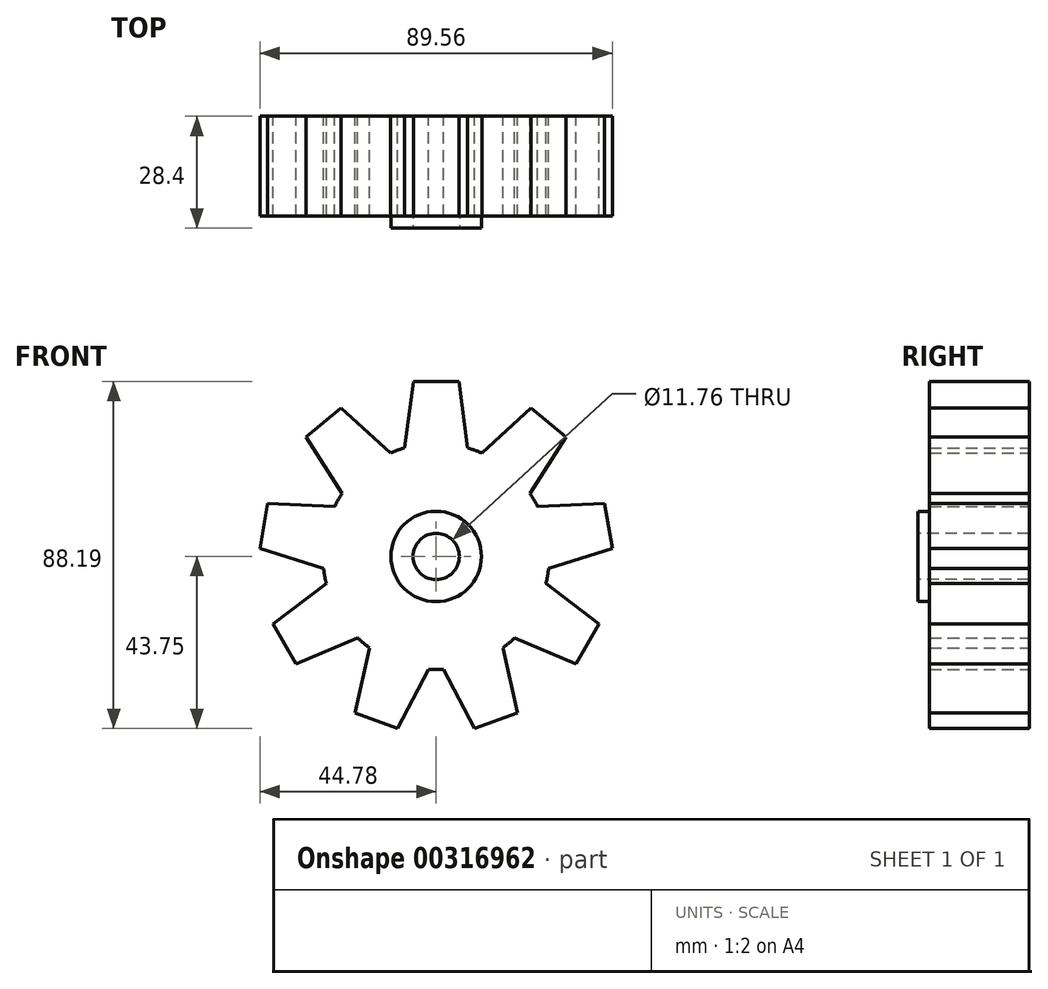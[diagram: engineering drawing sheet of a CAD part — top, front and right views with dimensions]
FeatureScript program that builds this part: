
annotation { "Feature Type Name" : "Feature", "Feature Type Description" : "" }
export const myFeature = defineFeature(function(context is Context, id is Id, definition is map)
    precondition{}
    {
        {
            var Q0;
            Q0=qCreatedBy(makeId("Front.planeOp"),FACE);
            var sketch = newSketch(context, id + "F0", { "sketchPlane" : qUnion([Q0])});
            skCircle(sketch, "E0", {"center": v(0, 0) * mm, "radius": 28.73 * mm});
            skLineSegment(sketch, "E1", {"start": v(0, 44.44) * mm, "end": v(0, 44.44) * mm});
            skLineSegment(sketch, "E2", {"start": v(0, 44.44) * mm, "end": v(5.8, 44.44) * mm});
            skLineSegment(sketch, "E3", {"start": v(5.8, 44.44) * mm, "end": v(8, 27.6) * mm});
            skLineSegment(sketch, "E4.MirrorCS", {"start": v(-5.8, 44.44) * mm, "end": v(-8, 27.6) * mm});
            skLineSegment(sketch, "E5.MirrorCS", {"start": v(0, 44.44) * mm, "end": v(-5.8, 44.44) * mm});
            skPoint(sketch, "E6.start.orphan", {"position": v(11.59, 0) * mm});
            skPoint(sketch, "E7.MirrorCS.start.orphan", {"position": v(-11.59, 0) * mm});
            skPoint(sketch, "E8.MirrorCS.start.orphan", {"position": v(0, 44.44) * mm});
            skLineSegment(sketch, "E9.1.0", {"start": v(28.57, 34.05) * mm, "end": v(33, 30.32) * mm});
            skLineSegment(sketch, "E9.1.1", {"start": v(33, 30.32) * mm, "end": v(23.86, 16) * mm});
            skLineSegment(sketch, "E9.1.2", {"start": v(24.13, 37.77) * mm, "end": v(11.62, 26.28) * mm});
            skLineSegment(sketch, "E9.1.3", {"start": v(28.57, 34.05) * mm, "end": v(24.13, 37.77) * mm});
            skLineSegment(sketch, "E9.2.0", {"start": v(43.77, 7.72) * mm, "end": v(44.78, 2) * mm});
            skLineSegment(sketch, "E9.2.1", {"start": v(44.78, 2) * mm, "end": v(28.57, -3.08) * mm});
            skLineSegment(sketch, "E9.2.2", {"start": v(42.76, 13.43) * mm, "end": v(25.8, 12.66) * mm});
            skLineSegment(sketch, "E9.2.3", {"start": v(43.77, 7.72) * mm, "end": v(42.76, 13.43) * mm});
            skLineSegment(sketch, "E9.3.0", {"start": v(38.5, -22.22) * mm, "end": v(35.6, -27.24) * mm});
            skLineSegment(sketch, "E9.3.1", {"start": v(35.6, -27.24) * mm, "end": v(19.9, -20.72) * mm});
            skLineSegment(sketch, "E9.3.2", {"start": v(41.39, -17.2) * mm, "end": v(27.9, -6.88) * mm});
            skLineSegment(sketch, "E9.3.3", {"start": v(38.5, -22.22) * mm, "end": v(41.39, -17.2) * mm});
            skLineSegment(sketch, "E9.4.0", {"start": v(15.2, -41.76) * mm, "end": v(9.75, -43.75) * mm});
            skLineSegment(sketch, "E9.4.1", {"start": v(9.75, -43.75) * mm, "end": v(1.93, -28.67) * mm});
            skLineSegment(sketch, "E9.4.2", {"start": v(20.65, -39.78) * mm, "end": v(16.95, -23.2) * mm});
            skLineSegment(sketch, "E9.4.3", {"start": v(15.2, -41.76) * mm, "end": v(20.65, -39.78) * mm});
            skLineSegment(sketch, "E9.5.0", {"start": v(-15.2, -41.76) * mm, "end": v(-20.65, -39.78) * mm});
            skLineSegment(sketch, "E9.5.1", {"start": v(-20.65, -39.78) * mm, "end": v(-16.95, -23.2) * mm});
            skLineSegment(sketch, "E9.5.2", {"start": v(-9.75, -43.75) * mm, "end": v(-1.93, -28.67) * mm});
            skLineSegment(sketch, "E9.5.3", {"start": v(-15.2, -41.76) * mm, "end": v(-9.75, -43.75) * mm});
            skLineSegment(sketch, "E9.6.0", {"start": v(-38.5, -22.22) * mm, "end": v(-41.39, -17.2) * mm});
            skLineSegment(sketch, "E9.6.1", {"start": v(-41.39, -17.2) * mm, "end": v(-27.9, -6.88) * mm});
            skLineSegment(sketch, "E9.6.2", {"start": v(-35.6, -27.24) * mm, "end": v(-19.9, -20.72) * mm});
            skLineSegment(sketch, "E9.6.3", {"start": v(-38.5, -22.22) * mm, "end": v(-35.6, -27.24) * mm});
            skLineSegment(sketch, "E9.7.0", {"start": v(-43.77, 7.72) * mm, "end": v(-42.76, 13.43) * mm});
            skLineSegment(sketch, "E9.7.1", {"start": v(-42.76, 13.43) * mm, "end": v(-25.8, 12.66) * mm});
            skLineSegment(sketch, "E9.7.2", {"start": v(-44.78, 2) * mm, "end": v(-28.57, -3.08) * mm});
            skLineSegment(sketch, "E9.7.3", {"start": v(-43.77, 7.72) * mm, "end": v(-44.78, 2) * mm});
            skLineSegment(sketch, "E9.8.0", {"start": v(-28.57, 34.05) * mm, "end": v(-24.13, 37.77) * mm});
            skLineSegment(sketch, "E9.8.1", {"start": v(-24.13, 37.77) * mm, "end": v(-11.62, 26.28) * mm});
            skLineSegment(sketch, "E9.8.2", {"start": v(-33, 30.32) * mm, "end": v(-23.86, 16) * mm});
            skLineSegment(sketch, "E9.8.3", {"start": v(-28.57, 34.05) * mm, "end": v(-33, 30.32) * mm});
            skLineSegment(sketch, "E9.anchor1", {"start": v(0, 0) * mm, "end": v(8, 27.6) * mm, "construction": true});
            skLineSegment(sketch, "E9.anchor2", {"start": v(0, 0) * mm, "end": v(8, 27.6) * mm, "construction": true});
            skSolve(sketch);
        }
        {
            var Q0;
            Q0 = qSketchRegion(id + "F0", true);
            extrude(context, id + "F1", {"entities" : qUnion([Q0]), "depth" : 25.4 * mm});
        }
        {
            var Q0;
            Q0=makeQuery(id+"F1.opExtrude","CAP_FACE",FACE,{"disambiguationData":[OSD([sQuery(id+"F0.wireOp",EDGE,"E0"),sQuery(id+"F0.wireOp",EDGE,"E9.1.0"),sQuery(id+"F0.wireOp",EDGE,"E9.1.1"),sQuery(id+"F0.wireOp",EDGE,"E9.1.2"),sQuery(id+"F0.wireOp",EDGE,"E9.1.3"),sQuery(id+"F0.wireOp",EDGE,"E9.2.0"),sQuery(id+"F0.wireOp",EDGE,"E9.2.1"),sQuery(id+"F0.wireOp",EDGE,"E9.2.2"),sQuery(id+"F0.wireOp",EDGE,"E9.2.3"),sQuery(id+"F0.wireOp",EDGE,"E9.3.0"),sQuery(id+"F0.wireOp",EDGE,"E9.3.1"),sQuery(id+"F0.wireOp",EDGE,"E9.3.2"),sQuery(id+"F0.wireOp",EDGE,"E9.3.3"),sQuery(id+"F0.wireOp",EDGE,"E9.4.0"),sQuery(id+"F0.wireOp",EDGE,"E9.4.1"),sQuery(id+"F0.wireOp",EDGE,"E9.4.2"),sQuery(id+"F0.wireOp",EDGE,"E9.4.3"),sQuery(id+"F0.wireOp",EDGE,"E9.5.0"),sQuery(id+"F0.wireOp",EDGE,"E9.5.1"),sQuery(id+"F0.wireOp",EDGE,"E9.5.2"),sQuery(id+"F0.wireOp",EDGE,"E9.5.3"),sQuery(id+"F0.wireOp",EDGE,"E9.6.0"),sQuery(id+"F0.wireOp",EDGE,"E9.6.1"),sQuery(id+"F0.wireOp",EDGE,"E9.6.2"),sQuery(id+"F0.wireOp",EDGE,"E9.6.3"),sQuery(id+"F0.wireOp",EDGE,"E9.7.0"),sQuery(id+"F0.wireOp",EDGE,"E9.7.1"),sQuery(id+"F0.wireOp",EDGE,"E9.7.2"),sQuery(id+"F0.wireOp",EDGE,"E9.7.3"),sQuery(id+"F0.wireOp",EDGE,"E9.8.0"),sQuery(id+"F0.wireOp",EDGE,"E9.8.1"),sQuery(id+"F0.wireOp",EDGE,"E9.8.2"),sQuery(id+"F0.wireOp",EDGE,"E9.8.3"),sQuery(id+"F0.wireOp",EDGE,"E2"),sQuery(id+"F0.wireOp",EDGE,"E3"),sQuery(id+"F0.wireOp",EDGE,"E4.MirrorCS"),sQuery(id+"F0.wireOp",EDGE,"E5.MirrorCS")])],"isStart":false});
            var sketch = newSketch(context, id + "F2", { "sketchPlane" : qUnion([Q0])});
            skCircle(sketch, "E10", {"center": v(0, 0) * mm, "radius": 11.49 * mm});
            skSolve(sketch);
        }
        {
            var Q0;
            Q0=makeQuery(id+"F2.imprint","IMPRINT",FACE,{"disambiguationData":[TD([[makeQuery(id+"F2.imprint","IMPRINT",EDGE,{"derivedFrom":sQuery(id+"F2.wireOp",EDGE,"E10")}),1.0]])]});
            extrude(context, id + "F3", {"entities" : qUnion([Q0]), "operationType" : NewBodyOperationType.ADD, "depth" : 3 * mm});
        }
        {
            var Q0;
            Q0=makeQuery(id+"F3.opExtrude","CAP_FACE",FACE,{"disambiguationData":[OSD([sQuery(id+"F2.wireOp",EDGE,"E10")])],"isStart":false});
            var sketch = newSketch(context, id + "F4", { "sketchPlane" : qUnion([Q0])});
            skCircle(sketch, "E11", {"center": v(0, 0) * mm, "radius": 5.88 * mm});
            skSolve(sketch);
        }
        {
            var Q0;
            Q0 = qSketchRegion(id + "F4", true);
            extrude(context, id + "F5", {"entities" : qUnion([Q0]), "operationType" : NewBodyOperationType.REMOVE, "endBound" : BoundingType.THROUGH_ALL, "oppositeDirection" : true, "depth" : 25.4 * mm});
        }
    });
